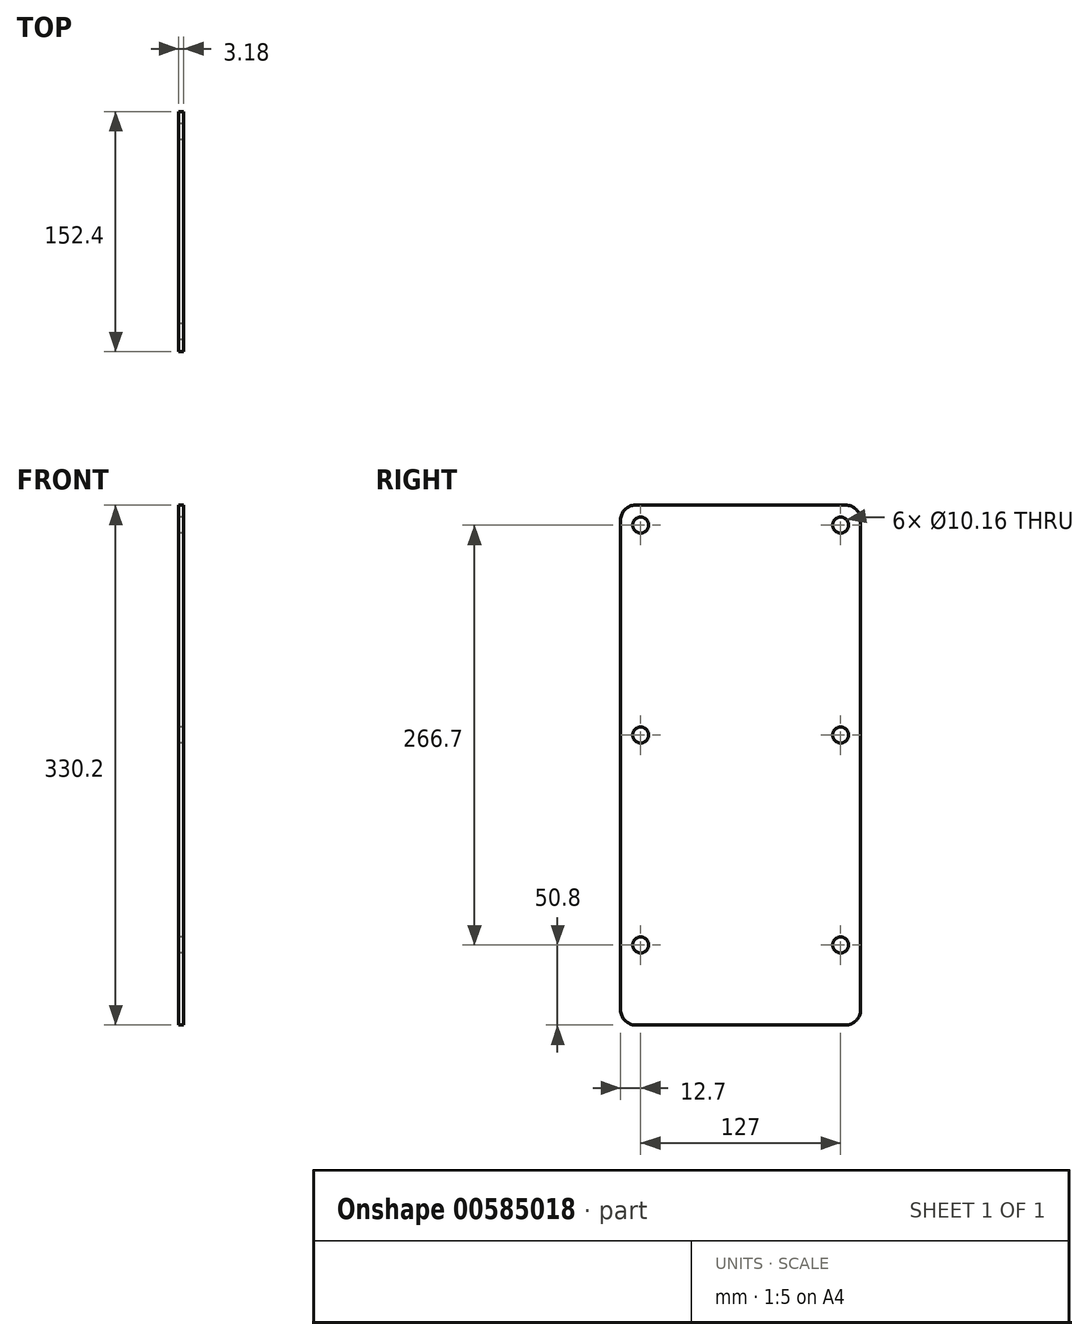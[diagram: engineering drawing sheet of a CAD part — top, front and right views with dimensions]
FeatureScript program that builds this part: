
annotation { "Feature Type Name" : "Feature", "Feature Type Description" : "" }
export const myFeature = defineFeature(function(context is Context, id is Id, definition is map)
    precondition{}
    {
        {
            var Q0;
            Q0=qCreatedBy(makeId("Right.planeOp"),FACE);
            var sketch = newSketch(context, id + "F0", { "sketchPlane" : qUnion([Q0])});
            skCircle(sketch, "E0", {"center": v(12.7, 50.8) * mm, "radius": 5.08 * mm});
            skLineSegment(sketch, "E1", {"start": v(152.4, 0) * mm, "end": v(152.4, 330.2) * mm});
            skLineSegment(sketch, "E2", {"start": v(152.4, 330.2) * mm, "end": v(0, 330.2) * mm});
            skLineSegment(sketch, "E3", {"start": v(0, 330.2) * mm, "end": v(0, 0) * mm});
            skLineSegment(sketch, "E4", {"start": v(0, 0) * mm, "end": v(152.4, 0) * mm});
            skCircle(sketch, "E5.0.1.0", {"center": v(12.7, 184.15) * mm, "radius": 5.08 * mm});
            skCircle(sketch, "E5.0.2.0", {"center": v(12.7, 317.5) * mm, "radius": 5.08 * mm});
            skCircle(sketch, "E5.1.0.0", {"center": v(139.7, 50.8) * mm, "radius": 5.08 * mm});
            skCircle(sketch, "E5.1.1.0", {"center": v(139.7, 184.15) * mm, "radius": 5.08 * mm});
            skCircle(sketch, "E5.1.2.0", {"center": v(139.7, 317.5) * mm, "radius": 5.08 * mm});
            skLineSegment(sketch, "E5.direction1", {"start": v(12.7, 50.8) * mm, "end": v(139.7, 50.8) * mm, "construction": true});
            skLineSegment(sketch, "E5.direction2", {"start": v(12.7, 50.8) * mm, "end": v(12.7, 184.15) * mm, "construction": true});
            skSolve(sketch);
        }
        {
            var Q0;
            Q0 = qSketchRegion(id + "F0", true);
            extrude(context, id + "F1", {"entities" : qUnion([Q0]), "depth" : 3.17 * mm, "offsetDistance" : 25.4 * mm});
        }
        {
            var Q0;
            Q0=makeQuery(id+"F1.opExtrude","SWEPT_EDGE",EDGE,{"disambiguationData":[OSD([sQuery(id+"F0.wireOp",EDGE,"E1"),sQuery(id+"F0.wireOp",EDGE,"E2")])]});
            var Q1;
            Q1=makeQuery(id+"F1.opExtrude","SWEPT_EDGE",EDGE,{"disambiguationData":[OSD([sQuery(id+"F0.wireOp",EDGE,"E2"),sQuery(id+"F0.wireOp",EDGE,"E3")])]});
            var Q2;
            Q2=makeQuery(id+"F1.opExtrude","SWEPT_EDGE",EDGE,{"disambiguationData":[OSD([sQuery(id+"F0.wireOp",EDGE,"E3"),sQuery(id+"F0.wireOp",EDGE,"E4")])]});
            var Q3;
            Q3=makeQuery(id+"F1.opExtrude","SWEPT_EDGE",EDGE,{"disambiguationData":[OSD([sQuery(id+"F0.wireOp",EDGE,"E1"),sQuery(id+"F0.wireOp",EDGE,"E4")])]});
            fillet(context, id + "F2", {"entities" : qUnion([Q0, Q1, Q2, Q3]), "tangentPropagation" : true, "radius" : 9.52 * mm, "defaultsChanged" : false, "vertexSettings" : [], "allowEdgeOverflow" : false});
        }
    });
